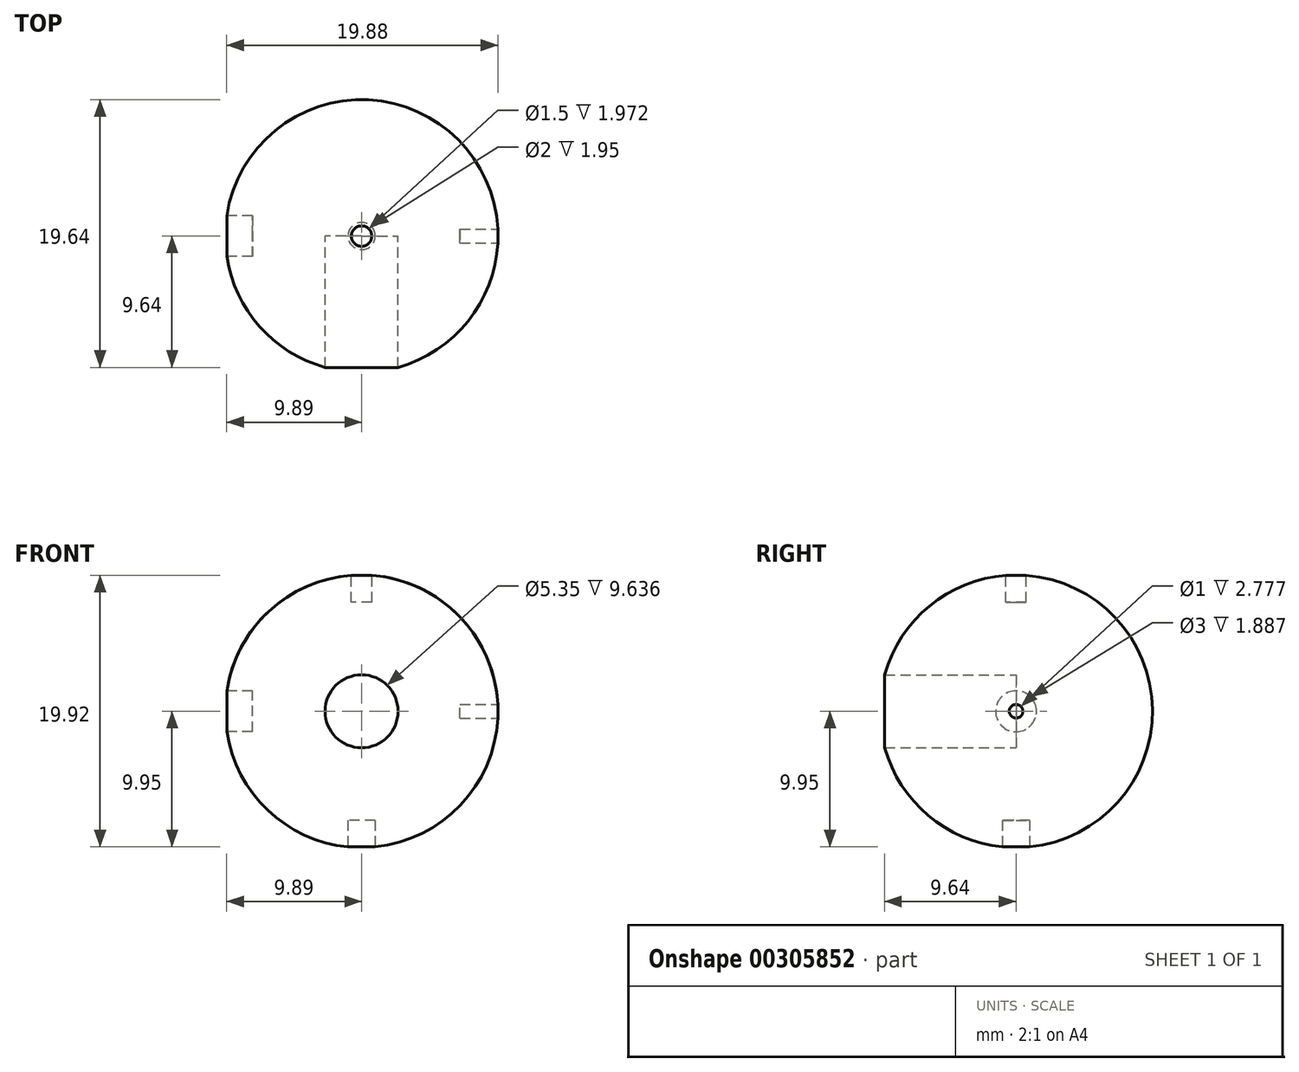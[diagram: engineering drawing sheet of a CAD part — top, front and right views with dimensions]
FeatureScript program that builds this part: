
annotation { "Feature Type Name" : "Feature", "Feature Type Description" : "" }
export const myFeature = defineFeature(function(context is Context, id is Id, definition is map)
    precondition{}
    {
        {
            var Q0;
            Q0=qCreatedBy(makeId("Front.planeOp"),FACE);
            var sketch = newSketch(context, id + "F0", { "sketchPlane" : qUnion([Q0])});
            skPoint(sketch, "E0.endSnap0", {"position": v(0, -12.5) * mm});
            skArc(sketch, "E1", {"start": v(-10, 0) * mm, "mid": v(0, -10) * mm, "end": v(10, 0) * mm});
            skLineSegment(sketch, "E2", {"start": v(-10, 0) * mm, "end": v(10, 0) * mm});
            skSolve(sketch);
        }
        {
            var Q0;
            Q0=makeQuery(id+"F0.imprint","IMPRINT",FACE,{"disambiguationData":[TD([[makeQuery(id+"F0.imprint","IMPRINT",EDGE,{"derivedFrom":sQuery(id+"F0.wireOp",EDGE,"E1")}),1.0]])]});
            var Q1;
            Q1=sQuery(id+"F0.wireOp",EDGE,"E2");
            revolve(context, id + "F1", {"entities" : qUnion([Q0]), "axis" : qUnion([Q1]), "revolveType" : RevolveType.FULL});
        }
        {
            var Q0;
            Q0=qCreatedBy(makeId("Front.planeOp"),FACE);
            var sketch = newSketch(context, id + "F2", { "sketchPlane" : qUnion([Q0])});
            skCircle(sketch, "E3", {"center": v(0, 0) * mm, "radius": 2.67 * mm});
            skSolve(sketch);
        }
        {
            var Q0;
            Q0=qSketchRegion(id+"F2",true);
            var Q1;
            Q1=sQuery(id+"F2.wireOp",EDGE,"E3");
            extrude(context, id + "F3", {"entities" : qUnion([Q0]), "operationType" : NewBodyOperationType.REMOVE, "surfaceEntities" : qUnion([Q1]), "depth" : 50 * mm});
        }
        {
            var Q0;
            Q0=qCreatedBy(makeId("Right.planeOp"),FACE);
            cPlane(context, id + "F4", {"entities" : qUnion([Q0]), "cplaneType" : CPlaneType.OFFSET, "offset" : 10 * mm, "width" : 150 * mm, "height" : 150 * mm});
        }
        {
            var Q0;
            Q0=qCreatedBy(makeId("Top.planeOp"),FACE);
            cPlane(context, id + "F5", {"entities" : qUnion([Q0]), "cplaneType" : CPlaneType.OFFSET, "offset" : 10 * mm, "width" : 150 * mm, "height" : 150 * mm});
        }
        {
            var Q0;
            Q0=qCreatedBy(makeId("Top.planeOp"),FACE);
            cPlane(context, id + "F6", {"entities" : qUnion([Q0]), "cplaneType" : CPlaneType.OFFSET, "offset" : 10 * mm, "oppositeDirection" : true, "width" : 150 * mm, "height" : 150 * mm});
        }
        {
            var Q0;
            Q0=qCreatedBy(makeId("Right.planeOp"),FACE);
            cPlane(context, id + "F7", {"entities" : qUnion([Q0]), "cplaneType" : CPlaneType.OFFSET, "offset" : 10 * mm, "oppositeDirection" : true, "width" : 150 * mm, "height" : 150 * mm});
        }
        {
            var Q0;
            Q0=qCreatedBy(id+"F4.planeOp",FACE);
            var sketch = newSketch(context, id + "F8", { "sketchPlane" : qUnion([Q0])});
            skCircle(sketch, "E4", {"center": v(0, 0) * mm, "radius": 0.5 * mm});
            skSolve(sketch);
        }
        {
            var Q0;
            Q0=qCreatedBy(id+"F5.planeOp",FACE);
            var sketch = newSketch(context, id + "F9", { "sketchPlane" : qUnion([Q0])});
            skCircle(sketch, "E5", {"center": v(0, 0) * mm, "radius": 0.75 * mm});
            skSolve(sketch);
        }
        {
            var Q0;
            Q0=qCreatedBy(id+"F6.planeOp",FACE);
            var sketch = newSketch(context, id + "F10", { "sketchPlane" : qUnion([Q0])});
            skCircle(sketch, "E6", {"center": v(0, 0) * mm, "radius": 1 * mm});
            skSolve(sketch);
        }
        {
            var Q0;
            Q0=qCreatedBy(id+"F7.planeOp",FACE);
            var sketch = newSketch(context, id + "F11", { "sketchPlane" : qUnion([Q0])});
            skCircle(sketch, "E7", {"center": v(0, 0) * mm, "radius": 1.5 * mm});
            skSolve(sketch);
        }
        {
            var Q0;
            Q0 = qSketchRegion(id + "F8", true);
            extrude(context, id + "F12", {"entities" : qUnion([Q0]), "operationType" : NewBodyOperationType.REMOVE, "endBound" : BoundingType.SYMMETRIC, "oppositeDirection" : true, "depth" : 5.58 * mm});
        }
        {
            var Q0;
            Q0 = qSketchRegion(id + "F9", true);
            extrude(context, id + "F13", {"entities" : qUnion([Q0]), "operationType" : NewBodyOperationType.REMOVE, "oppositeDirection" : true, "depth" : 2 * mm});
        }
        {
            var Q0;
            Q0 = qSketchRegion(id + "F10", true);
            extrude(context, id + "F14", {"entities" : qUnion([Q0]), "operationType" : NewBodyOperationType.REMOVE, "depth" : 2 * mm});
        }
        {
            var Q0;
            Q0 = qSketchRegion(id + "F11", true);
            extrude(context, id + "F15", {"entities" : qUnion([Q0]), "operationType" : NewBodyOperationType.REMOVE, "depth" : 2 * mm});
        }
    });
